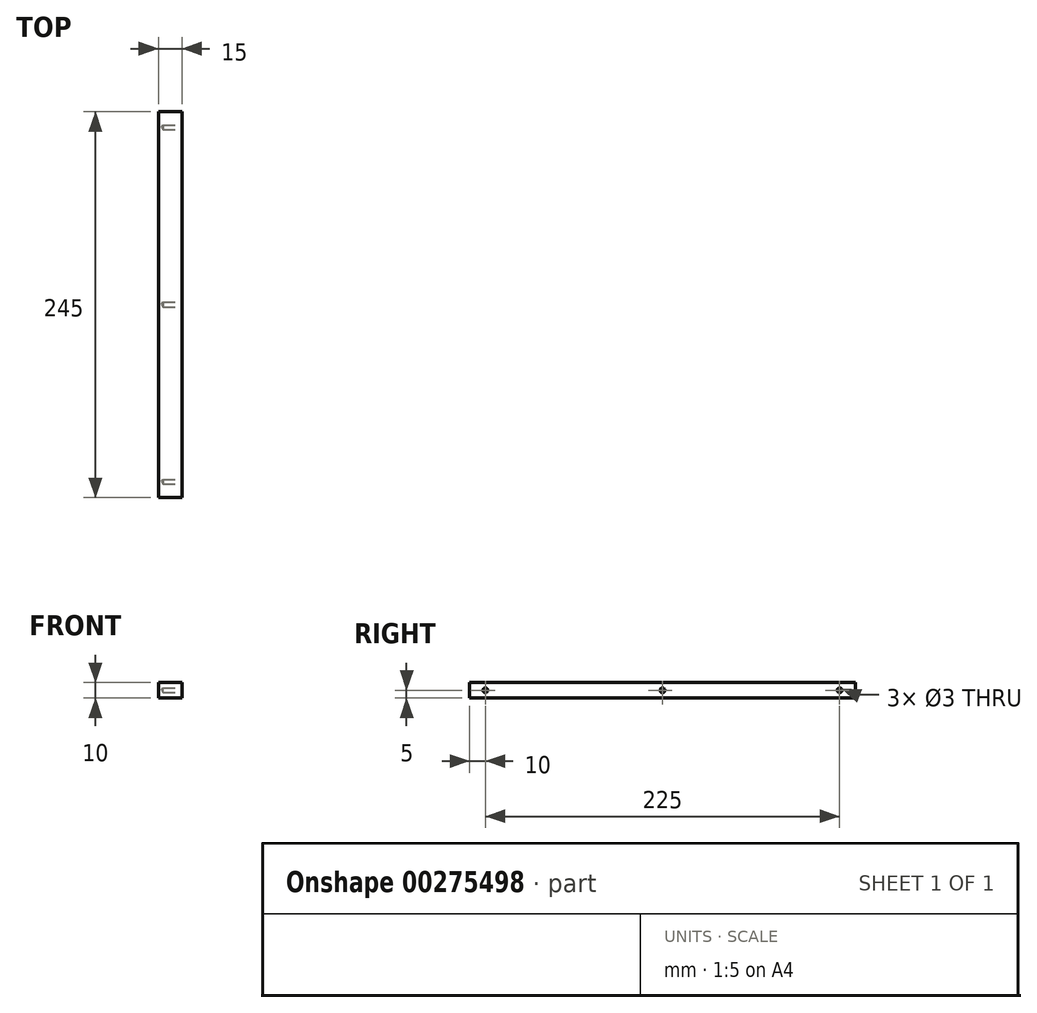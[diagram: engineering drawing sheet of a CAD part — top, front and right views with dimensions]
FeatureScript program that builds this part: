
annotation { "Feature Type Name" : "Feature", "Feature Type Description" : "" }
export const myFeature = defineFeature(function(context is Context, id is Id, definition is map)
    precondition{}
    {
        {
            var Q0;
            Q0=qCreatedBy(makeId("Top.planeOp"),FACE);
            var sketch = newSketch(context, id + "F0", { "sketchPlane" : qUnion([Q0])});
            skLineSegment(sketch, "E0.bottom", {"start": v(0, 0) * mm, "end": v(15, 0) * mm});
            skLineSegment(sketch, "E0.top", {"start": v(0, -245) * mm, "end": v(15, -245) * mm});
            skLineSegment(sketch, "E0.left", {"start": v(0, 0) * mm, "end": v(0, -245) * mm});
            skLineSegment(sketch, "E0.right", {"start": v(15, 0) * mm, "end": v(15, -245) * mm});
            skSolve(sketch);
        }
        {
            var Q0;
            Q0=makeQuery(id+"F0.imprint","IMPRINT",FACE,{"disambiguationData":[TD([[makeQuery(id+"F0.imprint","IMPRINT",EDGE,{"derivedFrom":sQuery(id+"F0.wireOp",EDGE,"E0.bottom")}),-1.0]])]});
            extrude(context, id + "F1", {"entities" : qUnion([Q0]), "depth" : 10 * mm});
        }
        {
            var Q0;
            Q0=makeQuery(id+"F1.opExtrude","SWEPT_FACE",FACE,{"disambiguationData":[OSD([sQuery(id+"F0.wireOp",EDGE,"E0.right")])]});
            var sketch = newSketch(context, id + "F2", { "sketchPlane" : qUnion([Q0])});
            skPoint(sketch, "E1", {"position": v(-235, 5) * mm});
            skPoint(sketch, "E2", {"position": v(-122.5, 5) * mm});
            skPoint(sketch, "E3", {"position": v(-10, 5) * mm});
            skSolve(sketch);
        }
        {
            var Q0;
            Q0=sQuery(id+"F2.wireOp",VERTEX,"E1");
            var Q1;
            Q1=sQuery(id+"F2.wireOp",VERTEX,"E2");
            var Q2;
            Q2=sQuery(id+"F2.wireOp",VERTEX,"E3");
            var Q3;
            Q3=makeQuery(id+"F1.opExtrude","SWEPT_BODY",BODY,{"disambiguationData":[OSD([sQuery(id+"F0.wireOp",EDGE,"E0.bottom"),sQuery(id+"F0.wireOp",EDGE,"E0.top"),sQuery(id+"F0.wireOp",EDGE,"E0.left"),sQuery(id+"F0.wireOp",EDGE,"E0.right")])]});
            hole(context, id + "F3", {"style" : HoleStyle.SIMPLE, "endStyle" : HoleEndStyle.BLIND, "holeDiameter" : 3 * mm, "holeDepth" : 12 * mm, "tappedDepth" : 12 * mm, "tapClearance" : 3, "locations" : qUnion([Q0, Q1, Q2]), "scope" : qUnion([Q3])});
        }
    });
